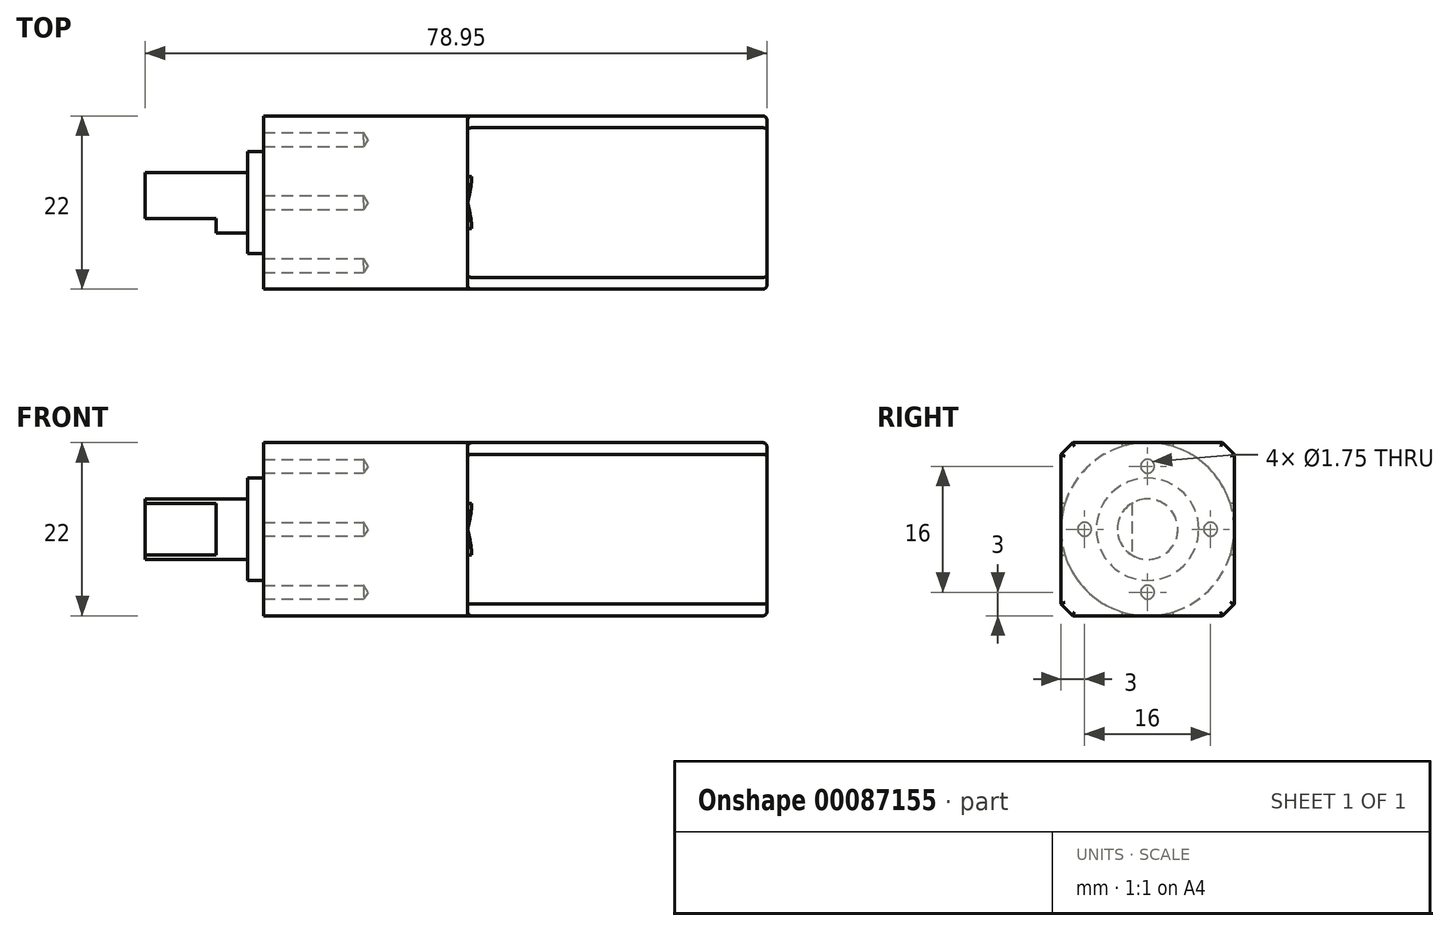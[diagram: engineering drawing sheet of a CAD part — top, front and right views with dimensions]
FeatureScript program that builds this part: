
annotation { "Feature Type Name" : "Feature", "Feature Type Description" : "" }
export const myFeature = defineFeature(function(context is Context, id is Id, definition is map)
    precondition{}
    {
        {
            var Q0;
            Q0=qCreatedBy(makeId("Right.planeOp"),FACE);
            var sketch = newSketch(context, id + "F0", { "sketchPlane" : qUnion([Q0])});
            skLineSegment(sketch, "E0.bottom", {"start": v(-11, 11) * mm, "end": v(11, 11) * mm});
            skLineSegment(sketch, "E0.top", {"start": v(-11, -11) * mm, "end": v(11, -11) * mm});
            skLineSegment(sketch, "E0.left", {"start": v(-11, 11) * mm, "end": v(-11, -11) * mm});
            skLineSegment(sketch, "E0.right", {"start": v(11, 11) * mm, "end": v(11, -11) * mm});
            skSolve(sketch);
        }
        {
            var Q0;
            Q0=makeQuery(id+"F0.imprint","IMPRINT",FACE,{"disambiguationData":[TD([[makeQuery(id+"F0.imprint","IMPRINT",EDGE,{"derivedFrom":sQuery(id+"F0.wireOp",EDGE,"E0.bottom")}),-1.0]])]});
            extrude(context, id + "F1", {"entities" : qUnion([Q0]), "depth" : 38 * mm, "offsetDistance" : 25 * mm});
        }
        {
            var Q0;
            Q0=makeQuery(id+"F1.opExtrude","CAP_FACE",FACE,{"disambiguationData":[OSD([sQuery(id+"F0.wireOp",EDGE,"E0.bottom"),sQuery(id+"F0.wireOp",EDGE,"E0.top"),sQuery(id+"F0.wireOp",EDGE,"E0.left"),sQuery(id+"F0.wireOp",EDGE,"E0.right")])],"isStart":true});
            var sketch = newSketch(context, id + "F2", { "sketchPlane" : qUnion([Q0])});
            skCircle(sketch, "E1", {"center": v(0, 0) * mm, "radius": 11 * mm});
            skSolve(sketch);
        }
        {
            var Q0;
            Q0 = qSketchRegion(id + "F2", true);
            extrude(context, id + "F3", {"entities" : qUnion([Q0]), "operationType" : NewBodyOperationType.ADD, "depth" : 25.95 * mm, "offsetDistance" : 25 * mm});
        }
        {
            var Q0;
            Q0=makeQuery(id+"F1.opExtrude","SWEPT_EDGE",EDGE,{"disambiguationData":[OSD([sQuery(id+"F0.wireOp",EDGE,"E0.bottom"),sQuery(id+"F0.wireOp",EDGE,"E0.left")])]});
            var Q1;
            Q1=makeQuery(id+"F1.opExtrude","SWEPT_EDGE",EDGE,{"disambiguationData":[OSD([sQuery(id+"F0.wireOp",EDGE,"E0.bottom"),sQuery(id+"F0.wireOp",EDGE,"E0.right")])]});
            var Q2;
            Q2=makeQuery(id+"F1.opExtrude","SWEPT_EDGE",EDGE,{"disambiguationData":[OSD([sQuery(id+"F0.wireOp",EDGE,"E0.top"),sQuery(id+"F0.wireOp",EDGE,"E0.right")])]});
            var Q3;
            Q3=makeQuery(id+"F1.opExtrude","SWEPT_EDGE",EDGE,{"disambiguationData":[OSD([sQuery(id+"F0.wireOp",EDGE,"E0.top"),sQuery(id+"F0.wireOp",EDGE,"E0.left")])]});
            chamfer(context, id + "F4", {"entities" : qUnion([Q0, Q1, Q2, Q3]), "width" : 1.5 * mm, "tangentPropagation" : true});
        }
        {
            var Q0;
            Q0=makeQuery(id+"F1.opExtrude","CAP_FACE",FACE,{"disambiguationData":[OSD([sQuery(id+"F0.wireOp",EDGE,"E0.bottom"),sQuery(id+"F0.wireOp",EDGE,"E0.top"),sQuery(id+"F0.wireOp",EDGE,"E0.left"),sQuery(id+"F0.wireOp",EDGE,"E0.right")])],"isStart":false});
            var Q1;
            {var subQ0=sQuery(id+"F0.wireOp",EDGE,"E0.right");var subQ1=sQuery(id+"F0.wireOp",EDGE,"E0.top");Q1=makeQuery(id+"F3.boolean.opBoolean","SPLIT",EDGE,{"disambiguationData":[TD([makeQuery(id+"F1.opExtrude","SWEPT_FACE",FACE,{"disambiguationData":[OSD([subQ0])]})])],"derivedFrom":makeQuery(id+"F1.opExtrude","CAP_EDGE",EDGE,{"disambiguationData":[OSD([subQ1])],"isStart":true})});}
            var Q2;
            {var subQ0=sQuery(id+"F0.wireOp",EDGE,"E0.right");var subQ1=sQuery(id+"F0.wireOp",EDGE,"E0.top");var subQ2=makeQuery(id+"F1.opExtrude","CAP_FACE",FACE,{"disambiguationData":[OSD([sQuery(id+"F0.wireOp",EDGE,"E0.bottom"),subQ1,sQuery(id+"F0.wireOp",EDGE,"E0.left"),subQ0])],"isStart":true});Q2=makeQuery(id+"F4.opChamfer","BLEND_EDGE",EDGE,{"blendedFrom":[makeQuery(id+"F1.opExtrude","SWEPT_EDGE",EDGE,{"disambiguationData":[OSD([subQ1,subQ0])]}),makeQuery(id+"F3.boolean.opBoolean","SPLIT",FACE,{"disambiguationData":[TD([subQ2,makeQuery(id+"F1.opExtrude","SWEPT_FACE",FACE,{"disambiguationData":[OSD([subQ1])]}),makeQuery(id+"F1.opExtrude","SWEPT_FACE",FACE,{"disambiguationData":[OSD([subQ0])]}),makeQuery(id+"F3.opExtrude","SWEPT_FACE",FACE,{"disambiguationData":[OSD([sQuery(id+"F2.wireOp",EDGE,"E1")])]})])],"derivedFrom":subQ2})],"blendedInto":[makeQuery(id+"F3.boolean.opBoolean","SPLIT",FACE,{"disambiguationData":[TD([subQ2,makeQuery(id+"F1.opExtrude","SWEPT_FACE",FACE,{"disambiguationData":[OSD([subQ1])]}),makeQuery(id+"F1.opExtrude","SWEPT_FACE",FACE,{"disambiguationData":[OSD([subQ0])]}),makeQuery(id+"F3.opExtrude","SWEPT_FACE",FACE,{"disambiguationData":[OSD([sQuery(id+"F2.wireOp",EDGE,"E1")])]})])],"derivedFrom":subQ2})]});}
            var Q3;
            {var subQ0=sQuery(id+"F0.wireOp",EDGE,"E0.right");var subQ1=sQuery(id+"F0.wireOp",EDGE,"E0.top");Q3=makeQuery(id+"F3.boolean.opBoolean","SPLIT",EDGE,{"disambiguationData":[TD([makeQuery(id+"F1.opExtrude","SWEPT_FACE",FACE,{"disambiguationData":[OSD([subQ1])]})])],"derivedFrom":makeQuery(id+"F1.opExtrude","CAP_EDGE",EDGE,{"disambiguationData":[OSD([subQ0])],"isStart":true})});}
            var Q4;
            {var subQ0=sQuery(id+"F0.wireOp",EDGE,"E0.bottom");var subQ1=sQuery(id+"F0.wireOp",EDGE,"E0.right");Q4=makeQuery(id+"F3.boolean.opBoolean","SPLIT",EDGE,{"disambiguationData":[TD([makeQuery(id+"F1.opExtrude","SWEPT_FACE",FACE,{"disambiguationData":[OSD([subQ1])]})])],"derivedFrom":makeQuery(id+"F1.opExtrude","CAP_EDGE",EDGE,{"disambiguationData":[OSD([subQ0])],"isStart":true})});}
            var Q5;
            {var subQ0=sQuery(id+"F0.wireOp",EDGE,"E0.bottom");var subQ1=sQuery(id+"F0.wireOp",EDGE,"E0.right");var subQ2=makeQuery(id+"F1.opExtrude","CAP_FACE",FACE,{"disambiguationData":[OSD([subQ0,sQuery(id+"F0.wireOp",EDGE,"E0.top"),sQuery(id+"F0.wireOp",EDGE,"E0.left"),subQ1])],"isStart":true});Q5=makeQuery(id+"F4.opChamfer","BLEND_EDGE",EDGE,{"blendedFrom":[makeQuery(id+"F1.opExtrude","SWEPT_EDGE",EDGE,{"disambiguationData":[OSD([subQ0,subQ1])]}),makeQuery(id+"F3.boolean.opBoolean","SPLIT",FACE,{"disambiguationData":[TD([makeQuery(id+"F1.opExtrude","SWEPT_FACE",FACE,{"disambiguationData":[OSD([subQ0])]}),subQ2,makeQuery(id+"F1.opExtrude","SWEPT_FACE",FACE,{"disambiguationData":[OSD([subQ1])]}),makeQuery(id+"F3.opExtrude","SWEPT_FACE",FACE,{"disambiguationData":[OSD([sQuery(id+"F2.wireOp",EDGE,"E1")])]})])],"derivedFrom":subQ2})],"blendedInto":[makeQuery(id+"F3.boolean.opBoolean","SPLIT",FACE,{"disambiguationData":[TD([makeQuery(id+"F1.opExtrude","SWEPT_FACE",FACE,{"disambiguationData":[OSD([subQ0])]}),subQ2,makeQuery(id+"F1.opExtrude","SWEPT_FACE",FACE,{"disambiguationData":[OSD([subQ1])]}),makeQuery(id+"F3.opExtrude","SWEPT_FACE",FACE,{"disambiguationData":[OSD([sQuery(id+"F2.wireOp",EDGE,"E1")])]})])],"derivedFrom":subQ2})]});}
            var Q6;
            {var subQ0=sQuery(id+"F0.wireOp",EDGE,"E0.bottom");var subQ1=sQuery(id+"F0.wireOp",EDGE,"E0.left");var subQ2=makeQuery(id+"F1.opExtrude","CAP_FACE",FACE,{"disambiguationData":[OSD([subQ0,sQuery(id+"F0.wireOp",EDGE,"E0.top"),subQ1,sQuery(id+"F0.wireOp",EDGE,"E0.right")])],"isStart":true});Q6=makeQuery(id+"F4.opChamfer","BLEND_EDGE",EDGE,{"blendedFrom":[makeQuery(id+"F1.opExtrude","SWEPT_EDGE",EDGE,{"disambiguationData":[OSD([subQ0,subQ1])]}),makeQuery(id+"F3.boolean.opBoolean","SPLIT",FACE,{"disambiguationData":[TD([makeQuery(id+"F1.opExtrude","SWEPT_FACE",FACE,{"disambiguationData":[OSD([subQ0])]}),subQ2,makeQuery(id+"F1.opExtrude","SWEPT_FACE",FACE,{"disambiguationData":[OSD([subQ1])]}),makeQuery(id+"F3.opExtrude","SWEPT_FACE",FACE,{"disambiguationData":[OSD([sQuery(id+"F2.wireOp",EDGE,"E1")])]})])],"derivedFrom":subQ2})],"blendedInto":[makeQuery(id+"F3.boolean.opBoolean","SPLIT",FACE,{"disambiguationData":[TD([makeQuery(id+"F1.opExtrude","SWEPT_FACE",FACE,{"disambiguationData":[OSD([subQ0])]}),subQ2,makeQuery(id+"F1.opExtrude","SWEPT_FACE",FACE,{"disambiguationData":[OSD([subQ1])]}),makeQuery(id+"F3.opExtrude","SWEPT_FACE",FACE,{"disambiguationData":[OSD([sQuery(id+"F2.wireOp",EDGE,"E1")])]})])],"derivedFrom":subQ2})]});}
            var Q7;
            {var subQ0=sQuery(id+"F0.wireOp",EDGE,"E0.bottom");var subQ1=sQuery(id+"F0.wireOp",EDGE,"E0.left");Q7=makeQuery(id+"F3.boolean.opBoolean","SPLIT",EDGE,{"disambiguationData":[TD([makeQuery(id+"F1.opExtrude","SWEPT_FACE",FACE,{"disambiguationData":[OSD([subQ0])]})])],"derivedFrom":makeQuery(id+"F1.opExtrude","CAP_EDGE",EDGE,{"disambiguationData":[OSD([subQ1])],"isStart":true})});}
            var Q8;
            {var subQ0=sQuery(id+"F0.wireOp",EDGE,"E0.left");var subQ1=sQuery(id+"F0.wireOp",EDGE,"E0.top");var subQ2=makeQuery(id+"F1.opExtrude","CAP_FACE",FACE,{"disambiguationData":[OSD([sQuery(id+"F0.wireOp",EDGE,"E0.bottom"),subQ1,subQ0,sQuery(id+"F0.wireOp",EDGE,"E0.right")])],"isStart":true});Q8=makeQuery(id+"F4.opChamfer","BLEND_EDGE",EDGE,{"blendedFrom":[makeQuery(id+"F1.opExtrude","SWEPT_EDGE",EDGE,{"disambiguationData":[OSD([subQ1,subQ0])]}),makeQuery(id+"F3.boolean.opBoolean","SPLIT",FACE,{"disambiguationData":[TD([subQ2,makeQuery(id+"F1.opExtrude","SWEPT_FACE",FACE,{"disambiguationData":[OSD([subQ1])]}),makeQuery(id+"F1.opExtrude","SWEPT_FACE",FACE,{"disambiguationData":[OSD([subQ0])]}),makeQuery(id+"F3.opExtrude","SWEPT_FACE",FACE,{"disambiguationData":[OSD([sQuery(id+"F2.wireOp",EDGE,"E1")])]})])],"derivedFrom":subQ2})],"blendedInto":[makeQuery(id+"F3.boolean.opBoolean","SPLIT",FACE,{"disambiguationData":[TD([subQ2,makeQuery(id+"F1.opExtrude","SWEPT_FACE",FACE,{"disambiguationData":[OSD([subQ1])]}),makeQuery(id+"F1.opExtrude","SWEPT_FACE",FACE,{"disambiguationData":[OSD([subQ0])]}),makeQuery(id+"F3.opExtrude","SWEPT_FACE",FACE,{"disambiguationData":[OSD([sQuery(id+"F2.wireOp",EDGE,"E1")])]})])],"derivedFrom":subQ2})]});}
            fillet(context, id + "F5", {"entities" : qUnion([Q0, Q1, Q2, Q3, Q4, Q5, Q6, Q7, Q8]), "radius" : .5 * mm, "tangentPropagation" : true, "allowEdgeOverflow" : false});
        }
        {
            var Q0;
            Q0=makeQuery(id+"F3.opExtrude","CAP_FACE",FACE,{"disambiguationData":[OSD([sQuery(id+"F2.wireOp",EDGE,"E1")])],"isStart":false});
            var sketch = newSketch(context, id + "F6", { "sketchPlane" : qUnion([Q0])});
            skCircle(sketch, "E2.0", {"center": v(0, 0) * mm, "radius": 11 * mm, "construction": true});
            skCircle(sketch, "E3", {"center": v(0, 0) * mm, "radius": 6.5 * mm});
            skSolve(sketch);
        }
        {
            var Q0;
            Q0 = qSketchRegion(id + "F6", true);
            extrude(context, id + "F7", {"entities" : qUnion([Q0]), "operationType" : NewBodyOperationType.ADD, "depth" : 2 * mm, "offsetDistance" : 25 * mm});
        }
        {
            var Q0;
            Q0=makeQuery(id+"F7.opExtrude","CAP_FACE",FACE,{"disambiguationData":[OSD([sQuery(id+"F6.wireOp",EDGE,"E3")])],"isStart":false});
            var sketch = newSketch(context, id + "F8", { "sketchPlane" : qUnion([Q0])});
            skCircle(sketch, "E4.0", {"center": v(0, 0) * mm, "radius": 6.5 * mm, "construction": true});
            skCircle(sketch, "E5", {"center": v(0, 0) * mm, "radius": 3.84 * mm});
            skSolve(sketch);
        }
        {
            var Q0;
            Q0 = qSketchRegion(id + "F8", true);
            extrude(context, id + "F9", {"entities" : qUnion([Q0]), "operationType" : NewBodyOperationType.ADD, "depth" : 13 * mm, "offsetDistance" : 25 * mm});
        }
        {
            var Q0;
            Q0=qCreatedBy(makeId("Front.planeOp"),FACE);
            cPlane(context, id + "F10", {"entities" : qUnion([Q0]), "cplaneType" : CPlaneType.OFFSET, "offset" : 2 * mm, "width" : 150 * mm, "height" : 150 * mm});
        }
        {
            var Q0;
            Q0=qCreatedBy(id+"F10.planeOp",FACE);
            var sketch = newSketch(context, id + "F11", { "sketchPlane" : qUnion([Q0])});
            skLineSegment(sketch, "E6", {"start": v(-40.95, 3.28) * mm, "end": v(-27.95, 3.28) * mm, "construction": true});
            skLineSegment(sketch, "E7", {"start": v(-27.95, -3.28) * mm, "end": v(-40.95, -3.28) * mm, "construction": true});
            skLineSegment(sketch, "E8.bottom", {"start": v(-40.95, 3.28) * mm, "end": v(-31.95, 3.28) * mm});
            skLineSegment(sketch, "E8.top", {"start": v(-40.95, -3.28) * mm, "end": v(-31.95, -3.28) * mm});
            skLineSegment(sketch, "E8.left", {"start": v(-40.95, 3.28) * mm, "end": v(-40.95, -3.28) * mm});
            skLineSegment(sketch, "E8.right", {"start": v(-31.95, 3.28) * mm, "end": v(-31.95, -3.28) * mm});
            skSolve(sketch);
        }
        {
            var Q0;
            Q0 = qSketchRegion(id + "F11", true);
            extrude(context, id + "F12", {"entities" : qUnion([Q0]), "operationType" : NewBodyOperationType.REMOVE, "depth" : 25 * mm, "offsetDistance" : 25 * mm});
        }
        {
            var Q0;
            Q0=makeQuery(id+"F3.opExtrude","CAP_FACE",FACE,{"disambiguationData":[OSD([sQuery(id+"F2.wireOp",EDGE,"E1")])],"isStart":false});
            var sketch = newSketch(context, id + "F13", { "sketchPlane" : qUnion([Q0])});
            skCircle(sketch, "E9", {"center": v(0, 0) * mm, "radius": 8 * mm, "construction": true});
            skPoint(sketch, "E10", {"position": v(0, 8) * mm});
            skPoint(sketch, "E11", {"position": v(8, 0) * mm});
            skPoint(sketch, "E12", {"position": v(0, -8) * mm});
            skPoint(sketch, "E13", {"position": v(-8, 0) * mm});
            skSolve(sketch);
        }
        {
            var Q0;
            Q0=sQuery(id+"F13.wireOp",VERTEX,"E13");
            var Q1;
            Q1=sQuery(id+"F13.wireOp",VERTEX,"E10");
            var Q2;
            Q2=sQuery(id+"F13.wireOp",VERTEX,"E11");
            var Q3;
            Q3=sQuery(id+"F13.wireOp",VERTEX,"E12");
            var Q4;
            Q4=makeQuery(id+"F1.opExtrude","SWEPT_BODY",BODY,{"disambiguationData":[OSD([sQuery(id+"F0.wireOp",EDGE,"E0.bottom"),sQuery(id+"F0.wireOp",EDGE,"E0.top"),sQuery(id+"F0.wireOp",EDGE,"E0.left"),sQuery(id+"F0.wireOp",EDGE,"E0.right")])]});
            hole(context, id + "F14", {"style" : HoleStyle.C_SINK, "endStyle" : HoleEndStyle.BLIND, "standardTappedOrClearance" : lookupTablePath({ "standard" : "ISO", "engagement" : "75%", "pitch" : "0.25 mm", "size" : "M2", "type" : "Tapped" }), "standardBlindInLast" : lookupTablePath({ "standard" : "ISO", "fit" : "Normal", "engagement" : "75%", "pitch" : "0.25 mm", "size" : "M2", "type" : "Clearance & tapped" }), "holeDiameter" : 1.75 * mm, "cSinkDiameter" : 1.75 * mm, "cSinkAngle" : 90 * degree, "majorDiameter" : 2 * mm, "showTappedDepth" : true, "holeDepth" : 12.75 * mm, "tappedDepth" : 12 * mm, "tapClearance" : 3, "locations" : qUnion([Q0, Q1, Q2, Q3]), "scope" : qUnion([Q4])});
        }
    });
